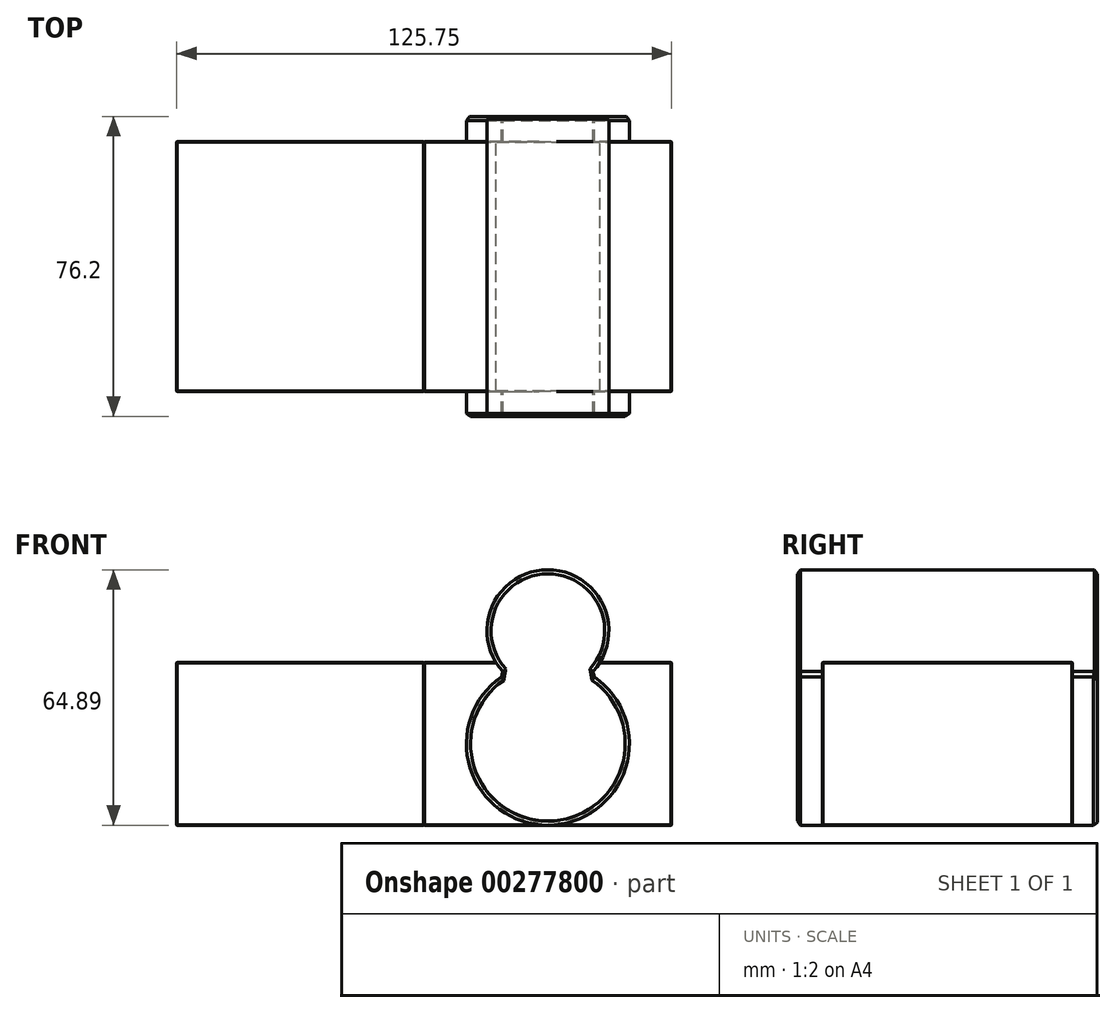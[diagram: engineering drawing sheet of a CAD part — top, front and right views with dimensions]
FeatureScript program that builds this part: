
annotation { "Feature Type Name" : "Feature", "Feature Type Description" : "" }
export const myFeature = defineFeature(function(context is Context, id is Id, definition is map)
    precondition{}
    {
        {
            var Q0;
            Q0=qCreatedBy(makeId("Front.planeOp"),FACE);
            var sketch = newSketch(context, id + "F0", { "sketchPlane" : qUnion([Q0])});
            skPoint(sketch, "E0.middle", {"position": v(0, 0) * mm});
            skLineSegment(sketch, "E1.bottom", {"start": v(-31.44, 20.7) * mm, "end": v(31.44, 20.7) * mm});
            skLineSegment(sketch, "E1.top", {"start": v(-31.44, -20.7) * mm, "end": v(31.44, -20.7) * mm});
            skLineSegment(sketch, "E1.left", {"start": v(-31.44, 20.7) * mm, "end": v(-31.44, -20.7) * mm});
            skLineSegment(sketch, "E1.right", {"start": v(31.44, 20.7) * mm, "end": v(31.44, -20.7) * mm});
            skSolve(sketch);
        }
        {
            var Q0;
            Q0 = qSketchRegion(id + "F0", true);
            extrude(context, id + "F1", {"entities" : qUnion([Q0]), "endBound" : BoundingType.SYMMETRIC, "depth" : 63.5 * mm});
        }
        {
            var Q0;
            Q0=qCreatedBy(makeId("Front.planeOp"),FACE);
            var sketch = newSketch(context, id + "F2", { "sketchPlane" : qUnion([Q0])});
            skCircle(sketch, "E2", {"center": v(0, 0) * mm, "radius": 20.69 * mm});
            skCircle(sketch, "E3", {"center": v(0, 28.72) * mm, "radius": 15.48 * mm});
            skSolve(sketch);
        }
        {
            var Q0;
            Q0 = qSketchRegion(id + "F2", true);
            extrude(context, id + "F3", {"entities" : qUnion([Q0]), "endBound" : BoundingType.SYMMETRIC, "depth" : 76.2 * mm});
        }
        {
            var Q0;
            Q0=makeQuery(id+"F3.opExtrude","SWEPT_FACE",FACE,{"disambiguationData":[OSD([sQuery(id+"F2.wireOp",EDGE,"E3")])]});
            var Q1;
            Q1=makeQuery(id+"F3.opExtrude","CAP_FACE",FACE,{"disambiguationData":[OSD([sQuery(id+"F2.wireOp",EDGE,"E2"),sQuery(id+"F2.wireOp",EDGE,"E3")])],"isStart":true});
            chamfer(context, id + "F4", {"entities" : qUnion([Q0, Q1]), "chamferType" : ChamferType.OFFSET_ANGLE, "width" : 1.27 * mm, "oppositeDirection" : false, "angle" : 45 * degree, "tangentPropagation" : true});
        }
        {
            var Q0;
            Q0=makeQuery(id+"F1.opExtrude","CAP_FACE",FACE,{"disambiguationData":[OSD([sQuery(id+"F0.wireOp",EDGE,"E1.bottom"),sQuery(id+"F0.wireOp",EDGE,"E1.top"),sQuery(id+"F0.wireOp",EDGE,"E1.left"),sQuery(id+"F0.wireOp",EDGE,"E1.right")])],"isStart":false});
            var Q1;
            Q1=makeQuery(id+"F1.opExtrude","SWEPT_FACE",FACE,{"disambiguationData":[OSD([sQuery(id+"F0.wireOp",EDGE,"E1.right")])]});
            var Q2;
            Q2=makeQuery(id+"F1.opExtrude","CAP_FACE",FACE,{"disambiguationData":[OSD([sQuery(id+"F0.wireOp",EDGE,"E1.bottom"),sQuery(id+"F0.wireOp",EDGE,"E1.top"),sQuery(id+"F0.wireOp",EDGE,"E1.left"),sQuery(id+"F0.wireOp",EDGE,"E1.right")])],"isStart":true});
            var Q3;
            Q3=makeQuery(id+"F1.opExtrude","SWEPT_FACE",FACE,{"disambiguationData":[OSD([sQuery(id+"F0.wireOp",EDGE,"E1.left")])]});
            chamfer(context, id + "F5", {"entities" : qUnion([Q0, Q1, Q2, Q3]), "chamferType" : ChamferType.OFFSET_ANGLE, "width" : 0.13 * mm, "oppositeDirection" : false, "angle" : 45 * degree, "tangentPropagation" : true});
        }
        {
            var Q0;
            Q0=makeQuery(id+"F1.opExtrude","SWEPT_BODY",BODY,{"disambiguationData":[OSD([sQuery(id+"F0.wireOp",EDGE,"E1.bottom"),sQuery(id+"F0.wireOp",EDGE,"E1.top"),sQuery(id+"F0.wireOp",EDGE,"E1.left"),sQuery(id+"F0.wireOp",EDGE,"E1.right")])]});
            var Q1;
            Q1=makeQuery(id+"F1.opExtrude","SWEPT_FACE",FACE,{"disambiguationData":[OSD([sQuery(id+"F0.wireOp",EDGE,"E1.left")])]});
            mirror(context, id + "F6", {"operationType" : NewBodyOperationType.ADD, "entities" : qUnion([Q0]), "mirrorPlane" : qUnion([Q1])});
        }
    });
